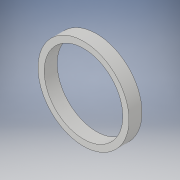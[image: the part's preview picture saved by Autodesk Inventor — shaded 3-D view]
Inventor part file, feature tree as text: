
AUTODESK INVENTOR PART (.ipt)
format: ipt  version: 2019 (Build 230136000, 136)  size: 105,472 bytes
history: native  units: mm
features: extrude x2, sketch x2
ambient origin geometry x8: Origin, YZ Plane, XZ Plane, XY Plane, X Axis, Y Axis, Z Axis, Center Point
bodies: Solid1 (feature_tree)
feature tree (4):
  extrude  "Extrusion1"  Depth=100.0mm TaperAngle=0.0deg
  extrude  "Extrusion2"  Depth=10.0mm TaperAngle=0.0deg
  sketch  "Sketch1"  dims[d0=700.0mm d1=100.0mm d2=0.0mm]
  sketch  "Sketch2"  dims[d3=605.0mm d4=10.0mm d5=0.0mm]
